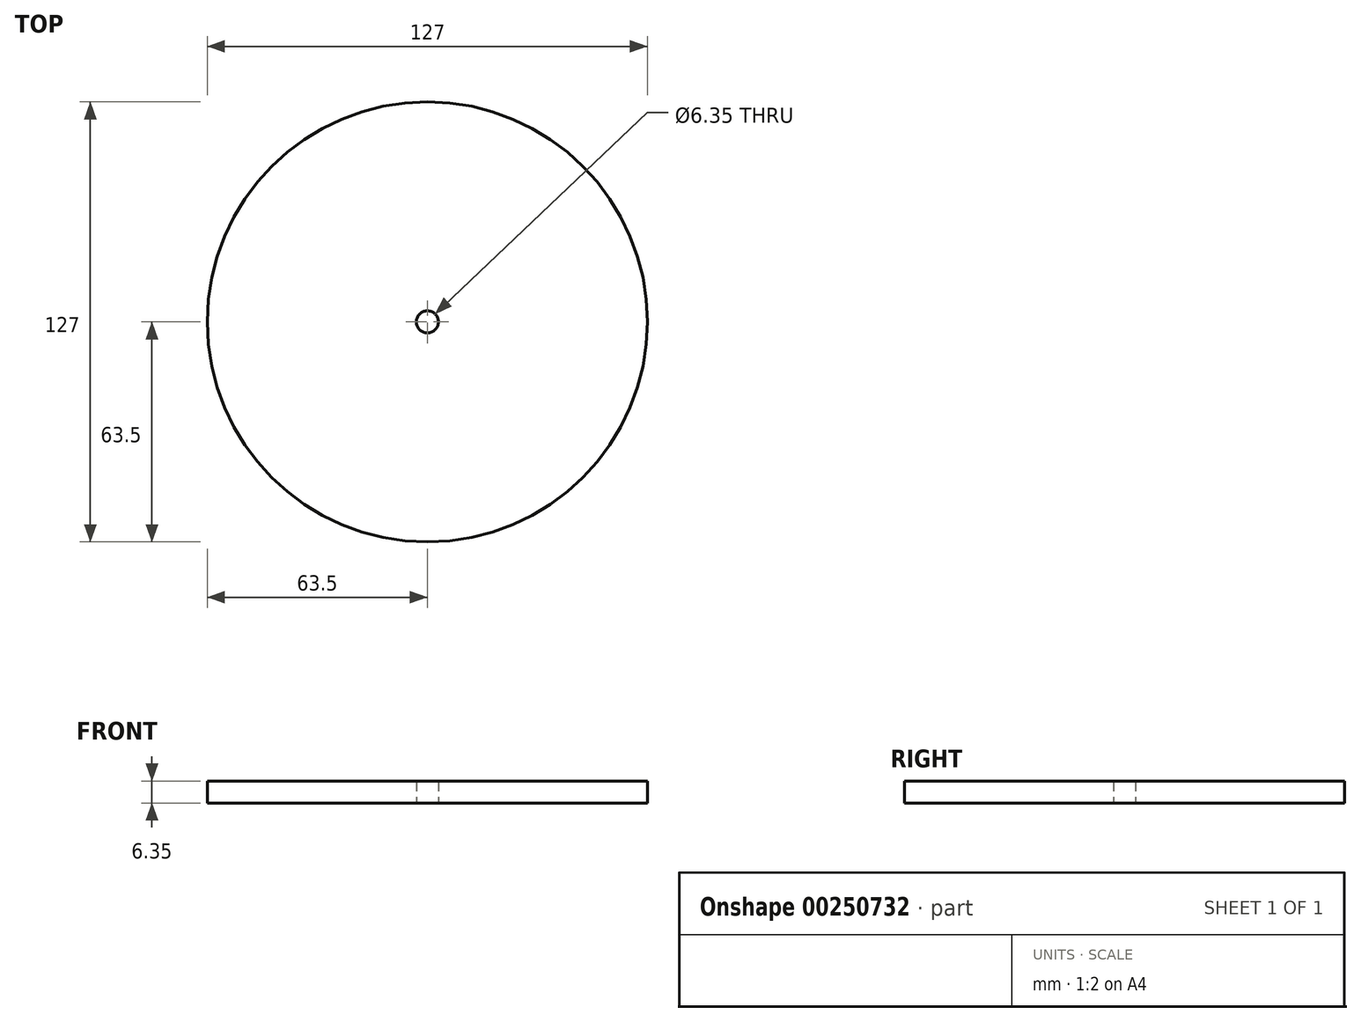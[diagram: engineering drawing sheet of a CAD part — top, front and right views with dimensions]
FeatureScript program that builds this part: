
annotation { "Feature Type Name" : "Feature", "Feature Type Description" : "" }
export const myFeature = defineFeature(function(context is Context, id is Id, definition is map)
    precondition{}
    {
        {
            var Q0;
            Q0=qCreatedBy(makeId("Top.planeOp"),FACE);
            var sketch = newSketch(context, id + "F0", { "sketchPlane" : qUnion([Q0])});
            skCircle(sketch, "E0", {"center": v(0, 0) * mm, "radius": 3.18 * mm});
            skCircle(sketch, "E1", {"center": v(0, 0) * mm, "radius": 63.5 * mm});
            skSolve(sketch);
        }
        {
            var Q0;
            Q0 = qSketchRegion(id + "F0", true);
            extrude(context, id + "F1", {"entities" : qUnion([Q0]), "depth" : 6.35 * mm});
        }
    });
